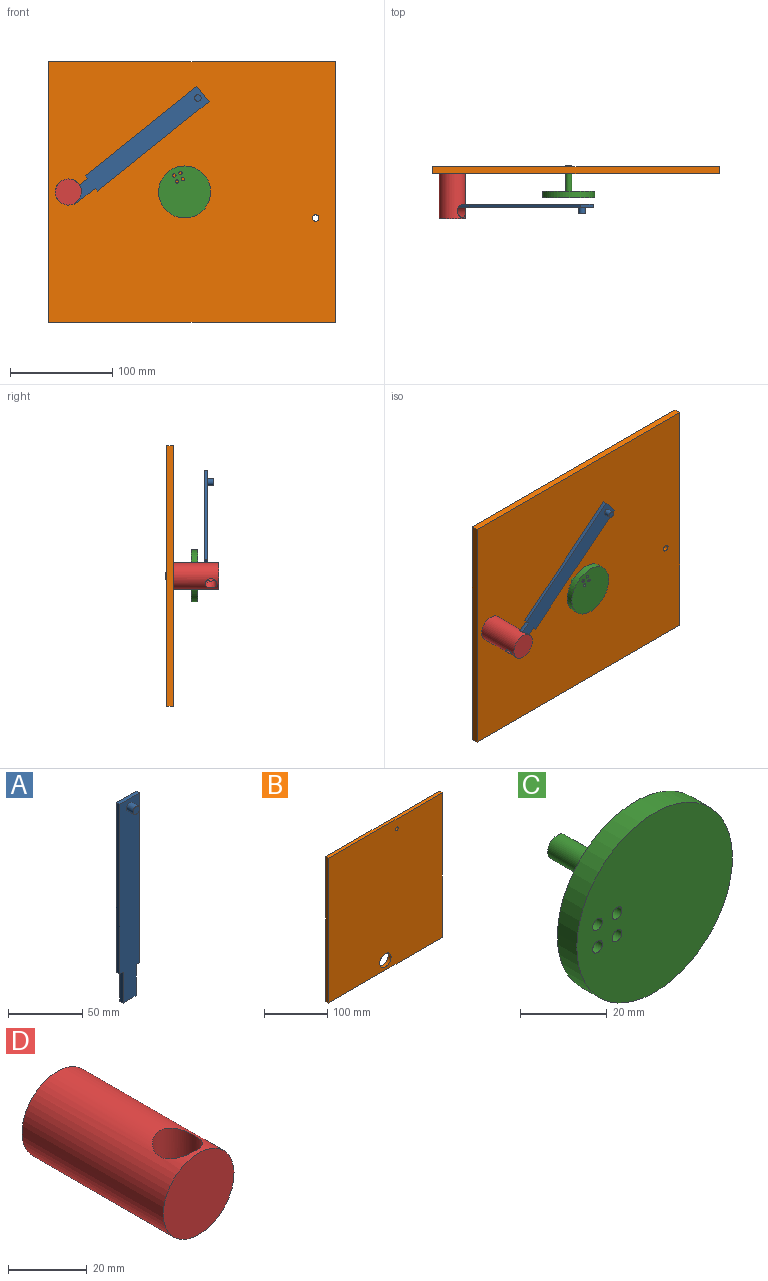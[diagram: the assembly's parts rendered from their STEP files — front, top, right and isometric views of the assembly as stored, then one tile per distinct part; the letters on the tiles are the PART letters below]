
ASSEMBLY  parts=4 mates=3
PART A: 12 faces, bbox 19.1x9.5x165.1 mm
  f0: plane 12.7x3.18mm, normal (0,0,-1), area 39.9mm2, adj f1,f7,f10,f11
  f1: plane 165.1x19.05mm, normal (0,-1,0), area 2942mm2, adj f0,f2,f3,f4,f5,f6,f8,f10
  f2: plane 139.7x3.18mm, normal (-1,0,0), area 443.5mm2, adj f1,f3,f6,f7
  f3: plane 3.38x3.18mm, normal (0,0,-1), area 10.3mm2, adj f1,f2,f7,f11
  f4: plane 3.38x3.18mm, normal (0,0,-1), area 10.3mm2, adj f1,f5,f7,f10
  f5: plane 139.7x3.18mm, normal (1,0,0), area 443.5mm2, adj f1,f4,f6,f7
  f6: plane 19.05x3.18mm, normal (0,0,1), area 60.5mm2, adj f1,f2,f5,f7
  f7: plane 165.1x19.05mm, normal (0,1,0), area 2973.6mm2, adj f0,f2,f3,f4,f5,f6,f10,f11
  f8: cylinder r=3.17mm len=6.35mm, axis (0,1,0), area 126.7mm2, adj f1,f9
  f9: plane 6.35x6.35mm, normal (0,-1,0), area 31.7mm2, adj f8
  f10: cylinder r=6.35mm len=25.4mm, axis (0,0,-1), area 81.5mm2, adj f0,f1,f4,f7
  f11: cylinder r=6.35mm len=25.4mm, axis (0,0,-1), area 81.5mm2, adj f0,f1,f3,f7
PART B: 8 faces, bbox 254x6.4x279.4 mm
  f0: plane 254x6.35mm, normal (0,0,1), area 1612.9mm2, adj f1,f5,f6,f7
  f1: plane 279.4x6.35mm, normal (-1,0,0), area 1774.2mm2, adj f0,f2,f6,f7
  f2: plane 254x6.35mm, normal (0,0,-1), area 1612.9mm2, adj f1,f5,f6,f7
  f3: cylinder r=12.7mm len=25.4mm, axis (0,-1,0), area 506.7mm2, adj f6,f7
  f4: cylinder r=3.17mm len=6.35mm, axis (0,-1,0), area 126.7mm2, adj f6,f7
  f5: plane 279.4x6.35mm, normal (1,0,0), area 1774.2mm2, adj f0,f2,f6,f7
  f6: plane 279.4x254mm, normal (0,1,0), area 70429.2mm2, adj f0,f1,f2,f3,f4,f5
  f7: plane 279.4x254mm, normal (0,-1,0), area 70429.2mm2, adj f0,f1,f2,f3,f4,f5
PART C: 9 faces, bbox 50.8x31.8x50.8 mm
  f0: cylinder r=1.59mm len=6.35mm, axis (0,1,0), area 63.3mm2, adj f5,f6
  f1: cylinder r=1.59mm len=6.35mm, axis (0,1,0), area 63.3mm2, adj f5,f6
  f2: cylinder r=1.59mm len=6.35mm, axis (0,1,0), area 63.3mm2, adj f5,f6
  f3: cylinder r=1.59mm len=6.35mm, axis (0,1,0), area 63.3mm2, adj f5,f6
  f4: cylinder r=25.4mm len=50.8mm, axis (0,1,0), area 1013.4mm2, adj f5,f6
  f5: plane 50.8x50.8mm, normal (0,-1,0), area 1995.2mm2, adj f0,f1,f2,f3,f4
  f6: plane 50.8x50.8mm, normal (0,1,0), area 1963.5mm2, adj f0,f1,f2,f3,f4,f7
  f7: cylinder r=3.17mm len=25.4mm, axis (0,-1,0), area 506.7mm2, adj f6,f8
  f8: plane 6.35x6.35mm, normal (0,1,0), area 31.7mm2, adj f7
PART D: 5 faces, bbox 25.4x50.8x25.4 mm
  f0: cylinder r=12.7mm len=50.8mm, axis (0,1,0), area 3817.1mm2, adj f1,f2,f3,f4
  f1: plane 25.4x25.4mm, normal (0,-1,0), area 506.7mm2, adj f0
  f2: plane 25.4x25.4mm, normal (0,1,0), area 506.7mm2, adj f0
  f3: cone r=6.35mm half-angle=3deg, axis (0,0,1), area 456.5mm2, adj f0,f4
  f4: cylinder r=6.35mm len=12.7mm, axis (0,0,1), area 473.4mm2, adj f0,f3
PLACE A rot(axis=(0,1,0),51.3deg) t=(-117.22,-36.51,6.17)mm
PLACE B rot(axis=(0,1,0),90deg) t=(4.35,-6.35,-294.62)mm
PLACE C rot(axis=(0,1,0),68deg) t=(-8.08,-23.81,0)mm
PLACE D rot(axis=(0,1,0),51.3deg) t=(-121.46,0,-0.01)mm
MATE parallel A.f7 <-> D.f0  axis (0,1,0) through (-51.43,-36.51,46.62)mm
MATE planar B.f6 <-> D.f0  axis (0,1,0) through (0,0,0)mm
MATE cylindrical D.f0 <-> B.f3  axis (0,1,0) through (-121.46,0,-0.01)mm
